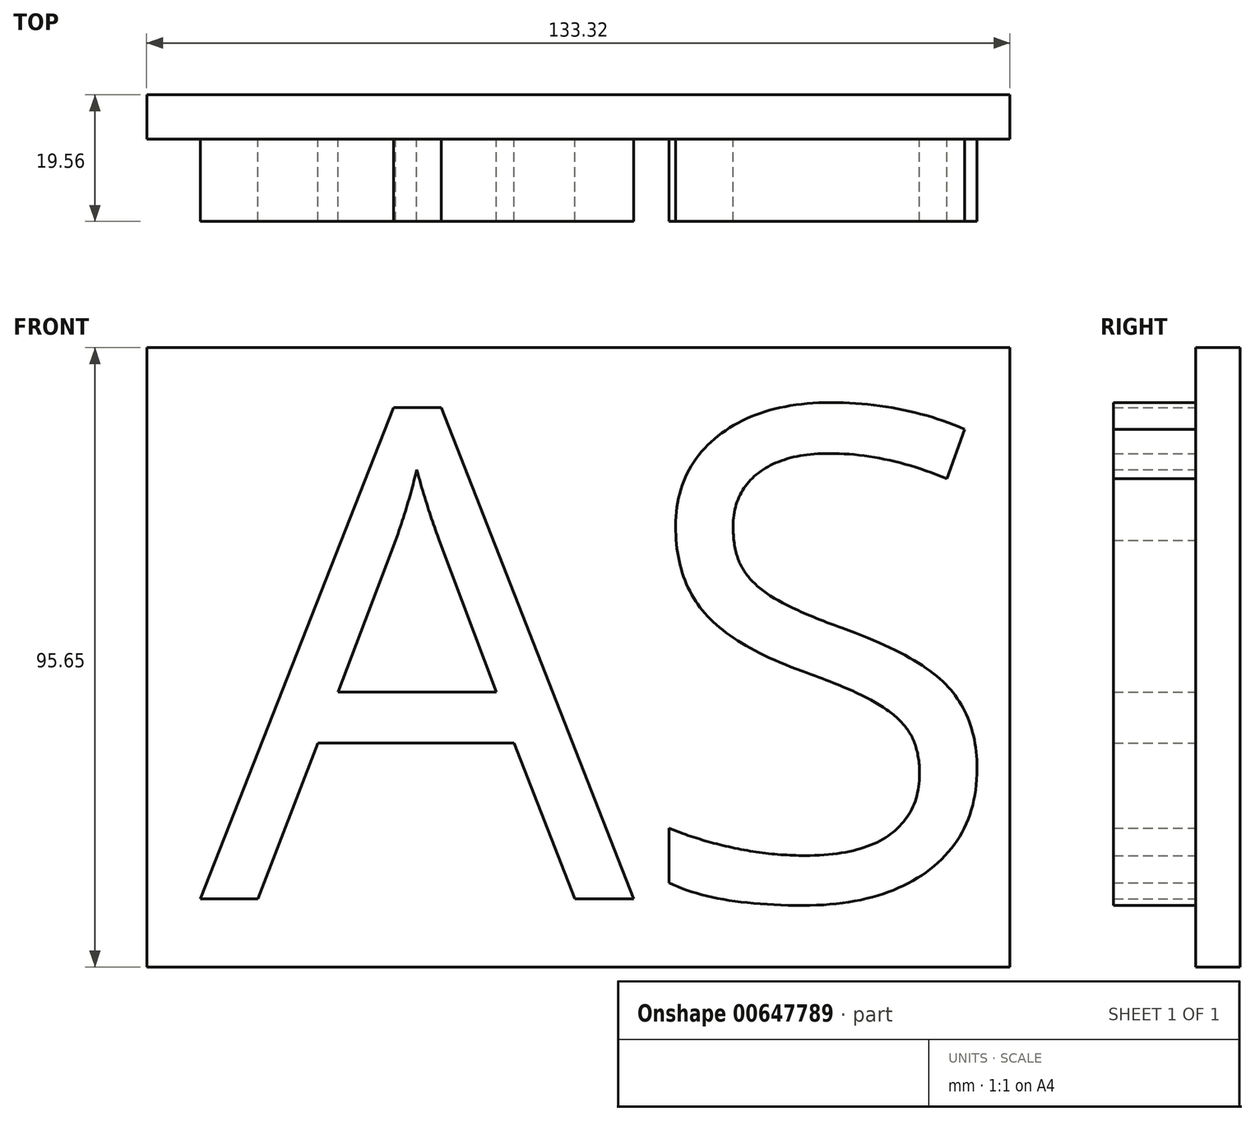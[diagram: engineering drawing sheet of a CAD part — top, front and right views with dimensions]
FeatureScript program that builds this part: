
annotation { "Feature Type Name" : "Feature", "Feature Type Description" : "" }
export const myFeature = defineFeature(function(context is Context, id is Id, definition is map)
    precondition{}
    {
        {
            var Q0;
            Q0=qCreatedBy(makeId("Front.planeOp"),FACE);
            var sketch = newSketch(context, id + "F0", { "sketchPlane" : qUnion([Q0])});
            skText(sketch, "E0", { "text": "AS", "fontName": "OpenSans-Regular.ttf"});
            const initialGuessF0  = {"E0": [-0.04475, -0.04426, 1, 0, 0.0762]};
            skSetInitialGuess(sketch, initialGuessF0);
            skSolve(sketch);
        }
        {
            var Q0;
            Q0 = qSketchRegion(id + "F0", true);
            extrude(context, id + "F1", {"entities" : qUnion([Q0]), "depth" : 12.7 * mm, "offsetDistance" : 25.4 * mm});
        }
        {
            var Q0;
            Q0=qCreatedBy(makeId("Front.planeOp"),FACE);
            var sketch = newSketch(context, id + "F2", { "sketchPlane" : qUnion([Q0])});
            skLineSegment(sketch, "E1.bottom", {"start": v(-53, 40.85) * mm, "end": v(80.3, 40.85) * mm});
            skLineSegment(sketch, "E1.top", {"start": v(-53, -54.8) * mm, "end": v(80.3, -54.8) * mm});
            skLineSegment(sketch, "E1.left", {"start": v(-53, 40.85) * mm, "end": v(-53, -54.8) * mm});
            skLineSegment(sketch, "E1.right", {"start": v(80.3, 40.85) * mm, "end": v(80.3, -54.8) * mm});
            skSolve(sketch);
        }
        {
            var Q0;
            Q0 = qSketchRegion(id + "F2", true);
            extrude(context, id + "F3", {"entities" : qUnion([Q0]), "operationType" : NewBodyOperationType.ADD, "oppositeDirection" : true, "depth" : 6.86 * mm, "offsetDistance" : 25.4 * mm});
        }
    });
